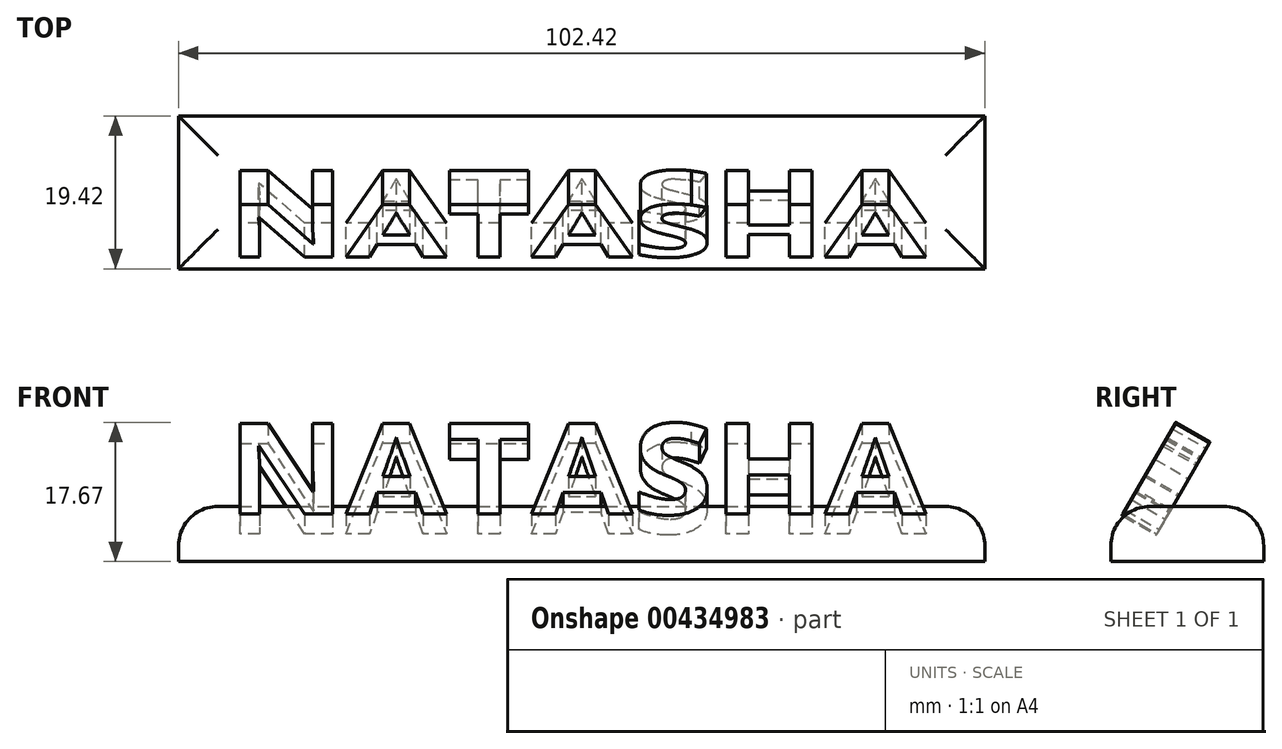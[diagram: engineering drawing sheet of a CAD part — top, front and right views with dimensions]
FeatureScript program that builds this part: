
annotation { "Feature Type Name" : "Feature", "Feature Type Description" : "" }
export const myFeature = defineFeature(function(context is Context, id is Id, definition is map)
    precondition{}
    {
        {
            var Q0;
            Q0=qCreatedBy(makeId("Top.planeOp"),FACE);
            var sketch = newSketch(context, id + "F0", { "sketchPlane" : qUnion([Q0])});
            skText(sketch, "E0", { "text": "NATASHA", "fontName": "OpenSans-Bold.ttf"});
            const initialGuessF0  = {"E0": [-0.03343, -0.0041, 1, 0, 0.01338]};
            skSetInitialGuess(sketch, initialGuessF0);
            skSolve(sketch);
        }
        {
            var Q0;
            Q0 = qSketchRegion(id + "F0", true);
            extrude(context, id + "F1", {"entities" : qUnion([Q0]), "depth" : 5 * mm});
        }
        {
            var Q0;
            Q0=qCreatedBy(makeId("Top.planeOp"),FACE);
            var sketch = newSketch(context, id + "F2", { "sketchPlane" : qUnion([Q0])});
            skLineSegment(sketch, "E1.bottom", {"start": v(-39.57, 31.58) * mm, "end": v(62.85, 31.58) * mm});
            skLineSegment(sketch, "E1.top", {"start": v(-39.57, 12.16) * mm, "end": v(62.85, 12.16) * mm});
            skLineSegment(sketch, "E1.left", {"start": v(-39.57, 31.58) * mm, "end": v(-39.57, 12.16) * mm});
            skLineSegment(sketch, "E1.right", {"start": v(62.85, 31.58) * mm, "end": v(62.85, 12.16) * mm});
            skSolve(sketch);
        }
        {
            var Q0;
            Q0=makeQuery(id+"F2.imprint","IMPRINT",FACE,{"disambiguationData":[TD([[makeQuery(id+"F2.imprint","IMPRINT",EDGE,{"derivedFrom":sQuery(id+"F2.wireOp",EDGE,"E1.bottom")}),-1.0]])]});
            extrude(context, id + "F3", {"entities" : qUnion([Q0]), "depth" : 7 * mm});
        }
        {
            var Q0;
            Q0=makeQuery(id+"F3.opExtrude","CAP_EDGE",EDGE,{"disambiguationData":[OSD([sQuery(id+"F2.wireOp",EDGE,"E1.left")])],"isStart":false});
            var Q1;
            Q1=makeQuery(id+"F3.opExtrude","CAP_EDGE",EDGE,{"disambiguationData":[OSD([sQuery(id+"F2.wireOp",EDGE,"E1.top")])],"isStart":false});
            var Q2;
            Q2=makeQuery(id+"F3.opExtrude","CAP_EDGE",EDGE,{"disambiguationData":[OSD([sQuery(id+"F2.wireOp",EDGE,"E1.right")])],"isStart":false});
            var Q3;
            Q3=makeQuery(id+"F3.opExtrude","CAP_EDGE",EDGE,{"disambiguationData":[OSD([sQuery(id+"F2.wireOp",EDGE,"E1.bottom")])],"isStart":false});
            fillet(context, id + "F4", {"entities" : qUnion([Q0, Q1, Q2, Q3]), "radius" : 5 * mm, "tangentPropagation" : true, "allowEdgeOverflow" : false});
        }
        {
            var Q0;
            Q0=makeQuery(id+"F1.opExtrude","SWEPT_BODY",BODY,{"disambiguationData":[OSD([sQuery(id+"F0.wireOp",EDGE,"E0.sketch_text.stroke-0"),sQuery(id+"F0.wireOp",EDGE,"E0.sketch_text.stroke-1"),sQuery(id+"F0.wireOp",EDGE,"E0.sketch_text.stroke-2"),sQuery(id+"F0.wireOp",EDGE,"E0.sketch_text.stroke-3"),sQuery(id+"F0.wireOp",EDGE,"E0.sketch_text.stroke-4"),sQuery(id+"F0.wireOp",EDGE,"E0.sketch_text.stroke-5"),sQuery(id+"F0.wireOp",EDGE,"E0.sketch_text.stroke-6"),sQuery(id+"F0.wireOp",EDGE,"E0.sketch_text.stroke-7"),sQuery(id+"F0.wireOp",EDGE,"E0.sketch_text.stroke-8"),sQuery(id+"F0.wireOp",EDGE,"E0.sketch_text.stroke-9"),sQuery(id+"F0.wireOp",EDGE,"E0.sketch_text.stroke-10"),sQuery(id+"F0.wireOp",EDGE,"E0.sketch_text.stroke-11"),sQuery(id+"F0.wireOp",EDGE,"E0.sketch_text.stroke-12"),sQuery(id+"F0.wireOp",EDGE,"E0.sketch_text.stroke-13")])]});
            var Q1;
            Q1=makeQuery(id+"F1.opExtrude","SWEPT_BODY",BODY,{"disambiguationData":[OSD([sQuery(id+"F0.wireOp",EDGE,"E0.sketch_text.stroke-14"),sQuery(id+"F0.wireOp",EDGE,"E0.sketch_text.stroke-15"),sQuery(id+"F0.wireOp",EDGE,"E0.sketch_text.stroke-16"),sQuery(id+"F0.wireOp",EDGE,"E0.sketch_text.stroke-17"),sQuery(id+"F0.wireOp",EDGE,"E0.sketch_text.stroke-18"),sQuery(id+"F0.wireOp",EDGE,"E0.sketch_text.stroke-19"),sQuery(id+"F0.wireOp",EDGE,"E0.sketch_text.stroke-20"),sQuery(id+"F0.wireOp",EDGE,"E0.sketch_text.stroke-21"),sQuery(id+"F0.wireOp",EDGE,"E0.sketch_text.stroke-22"),sQuery(id+"F0.wireOp",EDGE,"E0.sketch_text.stroke-23"),sQuery(id+"F0.wireOp",EDGE,"E0.sketch_text.stroke-24"),sQuery(id+"F0.wireOp",EDGE,"E0.sketch_text.stroke-25")])]});
            var Q2;
            Q2=makeQuery(id+"F1.opExtrude","SWEPT_BODY",BODY,{"disambiguationData":[OSD([sQuery(id+"F0.wireOp",EDGE,"E0.sketch_text.stroke-26"),sQuery(id+"F0.wireOp",EDGE,"E0.sketch_text.stroke-27"),sQuery(id+"F0.wireOp",EDGE,"E0.sketch_text.stroke-28"),sQuery(id+"F0.wireOp",EDGE,"E0.sketch_text.stroke-29"),sQuery(id+"F0.wireOp",EDGE,"E0.sketch_text.stroke-30"),sQuery(id+"F0.wireOp",EDGE,"E0.sketch_text.stroke-31"),sQuery(id+"F0.wireOp",EDGE,"E0.sketch_text.stroke-32"),sQuery(id+"F0.wireOp",EDGE,"E0.sketch_text.stroke-33")])]});
            var Q3;
            Q3=makeQuery(id+"F1.opExtrude","SWEPT_BODY",BODY,{"disambiguationData":[OSD([sQuery(id+"F0.wireOp",EDGE,"E0.sketch_text.stroke-34"),sQuery(id+"F0.wireOp",EDGE,"E0.sketch_text.stroke-35"),sQuery(id+"F0.wireOp",EDGE,"E0.sketch_text.stroke-36"),sQuery(id+"F0.wireOp",EDGE,"E0.sketch_text.stroke-37"),sQuery(id+"F0.wireOp",EDGE,"E0.sketch_text.stroke-38"),sQuery(id+"F0.wireOp",EDGE,"E0.sketch_text.stroke-39"),sQuery(id+"F0.wireOp",EDGE,"E0.sketch_text.stroke-40"),sQuery(id+"F0.wireOp",EDGE,"E0.sketch_text.stroke-41"),sQuery(id+"F0.wireOp",EDGE,"E0.sketch_text.stroke-42"),sQuery(id+"F0.wireOp",EDGE,"E0.sketch_text.stroke-43"),sQuery(id+"F0.wireOp",EDGE,"E0.sketch_text.stroke-44"),sQuery(id+"F0.wireOp",EDGE,"E0.sketch_text.stroke-45")])]});
            var Q4;
            Q4=makeQuery(id+"F1.opExtrude","SWEPT_BODY",BODY,{"disambiguationData":[OSD([sQuery(id+"F0.wireOp",EDGE,"E0.sketch_text.stroke-46"),sQuery(id+"F0.wireOp",EDGE,"E0.sketch_text.stroke-47"),sQuery(id+"F0.wireOp",EDGE,"E0.sketch_text.stroke-48"),sQuery(id+"F0.wireOp",EDGE,"E0.sketch_text.stroke-49"),sQuery(id+"F0.wireOp",EDGE,"E0.sketch_text.stroke-50"),sQuery(id+"F0.wireOp",EDGE,"E0.sketch_text.stroke-51"),sQuery(id+"F0.wireOp",EDGE,"E0.sketch_text.stroke-52"),sQuery(id+"F0.wireOp",EDGE,"E0.sketch_text.stroke-53"),sQuery(id+"F0.wireOp",EDGE,"E0.sketch_text.stroke-54"),sQuery(id+"F0.wireOp",EDGE,"E0.sketch_text.stroke-55"),sQuery(id+"F0.wireOp",EDGE,"E0.sketch_text.stroke-56"),sQuery(id+"F0.wireOp",EDGE,"E0.sketch_text.stroke-57"),sQuery(id+"F0.wireOp",EDGE,"E0.sketch_text.stroke-58"),sQuery(id+"F0.wireOp",EDGE,"E0.sketch_text.stroke-59"),sQuery(id+"F0.wireOp",EDGE,"E0.sketch_text.stroke-60"),sQuery(id+"F0.wireOp",EDGE,"E0.sketch_text.stroke-61"),sQuery(id+"F0.wireOp",EDGE,"E0.sketch_text.stroke-62"),sQuery(id+"F0.wireOp",EDGE,"E0.sketch_text.stroke-63"),sQuery(id+"F0.wireOp",EDGE,"E0.sketch_text.stroke-64"),sQuery(id+"F0.wireOp",EDGE,"E0.sketch_text.stroke-65"),sQuery(id+"F0.wireOp",EDGE,"E0.sketch_text.stroke-66"),sQuery(id+"F0.wireOp",EDGE,"E0.sketch_text.stroke-67"),sQuery(id+"F0.wireOp",EDGE,"E0.sketch_text.stroke-68"),sQuery(id+"F0.wireOp",EDGE,"E0.sketch_text.stroke-69"),sQuery(id+"F0.wireOp",EDGE,"E0.sketch_text.stroke-70"),sQuery(id+"F0.wireOp",EDGE,"E0.sketch_text.stroke-71"),sQuery(id+"F0.wireOp",EDGE,"E0.sketch_text.stroke-72"),sQuery(id+"F0.wireOp",EDGE,"E0.sketch_text.stroke-73")])]});
            var Q5;
            Q5=makeQuery(id+"F1.opExtrude","SWEPT_BODY",BODY,{"disambiguationData":[OSD([sQuery(id+"F0.wireOp",EDGE,"E0.sketch_text.stroke-74"),sQuery(id+"F0.wireOp",EDGE,"E0.sketch_text.stroke-75"),sQuery(id+"F0.wireOp",EDGE,"E0.sketch_text.stroke-76"),sQuery(id+"F0.wireOp",EDGE,"E0.sketch_text.stroke-77"),sQuery(id+"F0.wireOp",EDGE,"E0.sketch_text.stroke-78"),sQuery(id+"F0.wireOp",EDGE,"E0.sketch_text.stroke-79"),sQuery(id+"F0.wireOp",EDGE,"E0.sketch_text.stroke-80"),sQuery(id+"F0.wireOp",EDGE,"E0.sketch_text.stroke-81"),sQuery(id+"F0.wireOp",EDGE,"E0.sketch_text.stroke-82"),sQuery(id+"F0.wireOp",EDGE,"E0.sketch_text.stroke-83"),sQuery(id+"F0.wireOp",EDGE,"E0.sketch_text.stroke-84"),sQuery(id+"F0.wireOp",EDGE,"E0.sketch_text.stroke-85")])]});
            var Q6;
            Q6=makeQuery(id+"F1.opExtrude","SWEPT_BODY",BODY,{"disambiguationData":[OSD([sQuery(id+"F0.wireOp",EDGE,"E0.sketch_text.stroke-86"),sQuery(id+"F0.wireOp",EDGE,"E0.sketch_text.stroke-87"),sQuery(id+"F0.wireOp",EDGE,"E0.sketch_text.stroke-88"),sQuery(id+"F0.wireOp",EDGE,"E0.sketch_text.stroke-89"),sQuery(id+"F0.wireOp",EDGE,"E0.sketch_text.stroke-90"),sQuery(id+"F0.wireOp",EDGE,"E0.sketch_text.stroke-91"),sQuery(id+"F0.wireOp",EDGE,"E0.sketch_text.stroke-92"),sQuery(id+"F0.wireOp",EDGE,"E0.sketch_text.stroke-93"),sQuery(id+"F0.wireOp",EDGE,"E0.sketch_text.stroke-94"),sQuery(id+"F0.wireOp",EDGE,"E0.sketch_text.stroke-95"),sQuery(id+"F0.wireOp",EDGE,"E0.sketch_text.stroke-96"),sQuery(id+"F0.wireOp",EDGE,"E0.sketch_text.stroke-97")])]});
            var Q7;
            Q7=makeQuery(id+"F1.opExtrude","CAP_EDGE",EDGE,{"disambiguationData":[OSD([sQuery(id+"F0.wireOp",EDGE,"E0.sketch_text.stroke-26")])],"isStart":false});
            transform(context, id + "F5", {"entities" : qUnion([Q0, Q1, Q2, Q3, Q4, Q5, Q6]), "transformType" : TransformType.ROTATION, "transformAxis" : qUnion([Q7]), "angle" : 60 * degree, "oppositeDirection" : true, "makeCopy" : false});
        }
        {
            var Q0;
            Q0=makeQuery(id+"F1.opExtrude","SWEPT_BODY",BODY,{"disambiguationData":[OSD([sQuery(id+"F0.wireOp",EDGE,"E0.sketch_text.stroke-0"),sQuery(id+"F0.wireOp",EDGE,"E0.sketch_text.stroke-1"),sQuery(id+"F0.wireOp",EDGE,"E0.sketch_text.stroke-2"),sQuery(id+"F0.wireOp",EDGE,"E0.sketch_text.stroke-3"),sQuery(id+"F0.wireOp",EDGE,"E0.sketch_text.stroke-4"),sQuery(id+"F0.wireOp",EDGE,"E0.sketch_text.stroke-5"),sQuery(id+"F0.wireOp",EDGE,"E0.sketch_text.stroke-6"),sQuery(id+"F0.wireOp",EDGE,"E0.sketch_text.stroke-7"),sQuery(id+"F0.wireOp",EDGE,"E0.sketch_text.stroke-8"),sQuery(id+"F0.wireOp",EDGE,"E0.sketch_text.stroke-9"),sQuery(id+"F0.wireOp",EDGE,"E0.sketch_text.stroke-10"),sQuery(id+"F0.wireOp",EDGE,"E0.sketch_text.stroke-11"),sQuery(id+"F0.wireOp",EDGE,"E0.sketch_text.stroke-12"),sQuery(id+"F0.wireOp",EDGE,"E0.sketch_text.stroke-13")])]});
            var Q1;
            Q1=makeQuery(id+"F1.opExtrude","SWEPT_BODY",BODY,{"disambiguationData":[OSD([sQuery(id+"F0.wireOp",EDGE,"E0.sketch_text.stroke-14"),sQuery(id+"F0.wireOp",EDGE,"E0.sketch_text.stroke-15"),sQuery(id+"F0.wireOp",EDGE,"E0.sketch_text.stroke-16"),sQuery(id+"F0.wireOp",EDGE,"E0.sketch_text.stroke-17"),sQuery(id+"F0.wireOp",EDGE,"E0.sketch_text.stroke-18"),sQuery(id+"F0.wireOp",EDGE,"E0.sketch_text.stroke-19"),sQuery(id+"F0.wireOp",EDGE,"E0.sketch_text.stroke-20"),sQuery(id+"F0.wireOp",EDGE,"E0.sketch_text.stroke-21"),sQuery(id+"F0.wireOp",EDGE,"E0.sketch_text.stroke-22"),sQuery(id+"F0.wireOp",EDGE,"E0.sketch_text.stroke-23"),sQuery(id+"F0.wireOp",EDGE,"E0.sketch_text.stroke-24"),sQuery(id+"F0.wireOp",EDGE,"E0.sketch_text.stroke-25")])]});
            var Q2;
            Q2=makeQuery(id+"F1.opExtrude","SWEPT_BODY",BODY,{"disambiguationData":[OSD([sQuery(id+"F0.wireOp",EDGE,"E0.sketch_text.stroke-26"),sQuery(id+"F0.wireOp",EDGE,"E0.sketch_text.stroke-27"),sQuery(id+"F0.wireOp",EDGE,"E0.sketch_text.stroke-28"),sQuery(id+"F0.wireOp",EDGE,"E0.sketch_text.stroke-29"),sQuery(id+"F0.wireOp",EDGE,"E0.sketch_text.stroke-30"),sQuery(id+"F0.wireOp",EDGE,"E0.sketch_text.stroke-31"),sQuery(id+"F0.wireOp",EDGE,"E0.sketch_text.stroke-32"),sQuery(id+"F0.wireOp",EDGE,"E0.sketch_text.stroke-33")])]});
            var Q3;
            Q3=makeQuery(id+"F1.opExtrude","SWEPT_BODY",BODY,{"disambiguationData":[OSD([sQuery(id+"F0.wireOp",EDGE,"E0.sketch_text.stroke-34"),sQuery(id+"F0.wireOp",EDGE,"E0.sketch_text.stroke-35"),sQuery(id+"F0.wireOp",EDGE,"E0.sketch_text.stroke-36"),sQuery(id+"F0.wireOp",EDGE,"E0.sketch_text.stroke-37"),sQuery(id+"F0.wireOp",EDGE,"E0.sketch_text.stroke-38"),sQuery(id+"F0.wireOp",EDGE,"E0.sketch_text.stroke-39"),sQuery(id+"F0.wireOp",EDGE,"E0.sketch_text.stroke-40"),sQuery(id+"F0.wireOp",EDGE,"E0.sketch_text.stroke-41"),sQuery(id+"F0.wireOp",EDGE,"E0.sketch_text.stroke-42"),sQuery(id+"F0.wireOp",EDGE,"E0.sketch_text.stroke-43"),sQuery(id+"F0.wireOp",EDGE,"E0.sketch_text.stroke-44"),sQuery(id+"F0.wireOp",EDGE,"E0.sketch_text.stroke-45")])]});
            var Q4;
            Q4=makeQuery(id+"F1.opExtrude","SWEPT_BODY",BODY,{"disambiguationData":[OSD([sQuery(id+"F0.wireOp",EDGE,"E0.sketch_text.stroke-46"),sQuery(id+"F0.wireOp",EDGE,"E0.sketch_text.stroke-47"),sQuery(id+"F0.wireOp",EDGE,"E0.sketch_text.stroke-48"),sQuery(id+"F0.wireOp",EDGE,"E0.sketch_text.stroke-49"),sQuery(id+"F0.wireOp",EDGE,"E0.sketch_text.stroke-50"),sQuery(id+"F0.wireOp",EDGE,"E0.sketch_text.stroke-51"),sQuery(id+"F0.wireOp",EDGE,"E0.sketch_text.stroke-52"),sQuery(id+"F0.wireOp",EDGE,"E0.sketch_text.stroke-53"),sQuery(id+"F0.wireOp",EDGE,"E0.sketch_text.stroke-54"),sQuery(id+"F0.wireOp",EDGE,"E0.sketch_text.stroke-55"),sQuery(id+"F0.wireOp",EDGE,"E0.sketch_text.stroke-56"),sQuery(id+"F0.wireOp",EDGE,"E0.sketch_text.stroke-57"),sQuery(id+"F0.wireOp",EDGE,"E0.sketch_text.stroke-58"),sQuery(id+"F0.wireOp",EDGE,"E0.sketch_text.stroke-59"),sQuery(id+"F0.wireOp",EDGE,"E0.sketch_text.stroke-60"),sQuery(id+"F0.wireOp",EDGE,"E0.sketch_text.stroke-61"),sQuery(id+"F0.wireOp",EDGE,"E0.sketch_text.stroke-62"),sQuery(id+"F0.wireOp",EDGE,"E0.sketch_text.stroke-63"),sQuery(id+"F0.wireOp",EDGE,"E0.sketch_text.stroke-64"),sQuery(id+"F0.wireOp",EDGE,"E0.sketch_text.stroke-65"),sQuery(id+"F0.wireOp",EDGE,"E0.sketch_text.stroke-66"),sQuery(id+"F0.wireOp",EDGE,"E0.sketch_text.stroke-67"),sQuery(id+"F0.wireOp",EDGE,"E0.sketch_text.stroke-68"),sQuery(id+"F0.wireOp",EDGE,"E0.sketch_text.stroke-69"),sQuery(id+"F0.wireOp",EDGE,"E0.sketch_text.stroke-70"),sQuery(id+"F0.wireOp",EDGE,"E0.sketch_text.stroke-71"),sQuery(id+"F0.wireOp",EDGE,"E0.sketch_text.stroke-72"),sQuery(id+"F0.wireOp",EDGE,"E0.sketch_text.stroke-73")])]});
            var Q5;
            Q5=makeQuery(id+"F1.opExtrude","SWEPT_BODY",BODY,{"disambiguationData":[OSD([sQuery(id+"F0.wireOp",EDGE,"E0.sketch_text.stroke-74"),sQuery(id+"F0.wireOp",EDGE,"E0.sketch_text.stroke-75"),sQuery(id+"F0.wireOp",EDGE,"E0.sketch_text.stroke-76"),sQuery(id+"F0.wireOp",EDGE,"E0.sketch_text.stroke-77"),sQuery(id+"F0.wireOp",EDGE,"E0.sketch_text.stroke-78"),sQuery(id+"F0.wireOp",EDGE,"E0.sketch_text.stroke-79"),sQuery(id+"F0.wireOp",EDGE,"E0.sketch_text.stroke-80"),sQuery(id+"F0.wireOp",EDGE,"E0.sketch_text.stroke-81"),sQuery(id+"F0.wireOp",EDGE,"E0.sketch_text.stroke-82"),sQuery(id+"F0.wireOp",EDGE,"E0.sketch_text.stroke-83"),sQuery(id+"F0.wireOp",EDGE,"E0.sketch_text.stroke-84"),sQuery(id+"F0.wireOp",EDGE,"E0.sketch_text.stroke-85")])]});
            var Q6;
            Q6=makeQuery(id+"F1.opExtrude","SWEPT_BODY",BODY,{"disambiguationData":[OSD([sQuery(id+"F0.wireOp",EDGE,"E0.sketch_text.stroke-86"),sQuery(id+"F0.wireOp",EDGE,"E0.sketch_text.stroke-87"),sQuery(id+"F0.wireOp",EDGE,"E0.sketch_text.stroke-88"),sQuery(id+"F0.wireOp",EDGE,"E0.sketch_text.stroke-89"),sQuery(id+"F0.wireOp",EDGE,"E0.sketch_text.stroke-90"),sQuery(id+"F0.wireOp",EDGE,"E0.sketch_text.stroke-91"),sQuery(id+"F0.wireOp",EDGE,"E0.sketch_text.stroke-92"),sQuery(id+"F0.wireOp",EDGE,"E0.sketch_text.stroke-93"),sQuery(id+"F0.wireOp",EDGE,"E0.sketch_text.stroke-94"),sQuery(id+"F0.wireOp",EDGE,"E0.sketch_text.stroke-95"),sQuery(id+"F0.wireOp",EDGE,"E0.sketch_text.stroke-96"),sQuery(id+"F0.wireOp",EDGE,"E0.sketch_text.stroke-97")])]});
            transform(context, id + "F6", {"entities" : qUnion([Q0, Q1, Q2, Q3, Q4, Q5, Q6]), "transformType" : TransformType.TRANSLATION_3D, "dx" : 0 * mm, "dy" : 17.78 * mm, "dz" : 1.02 * mm, "makeCopy" : false});
        }
    });
